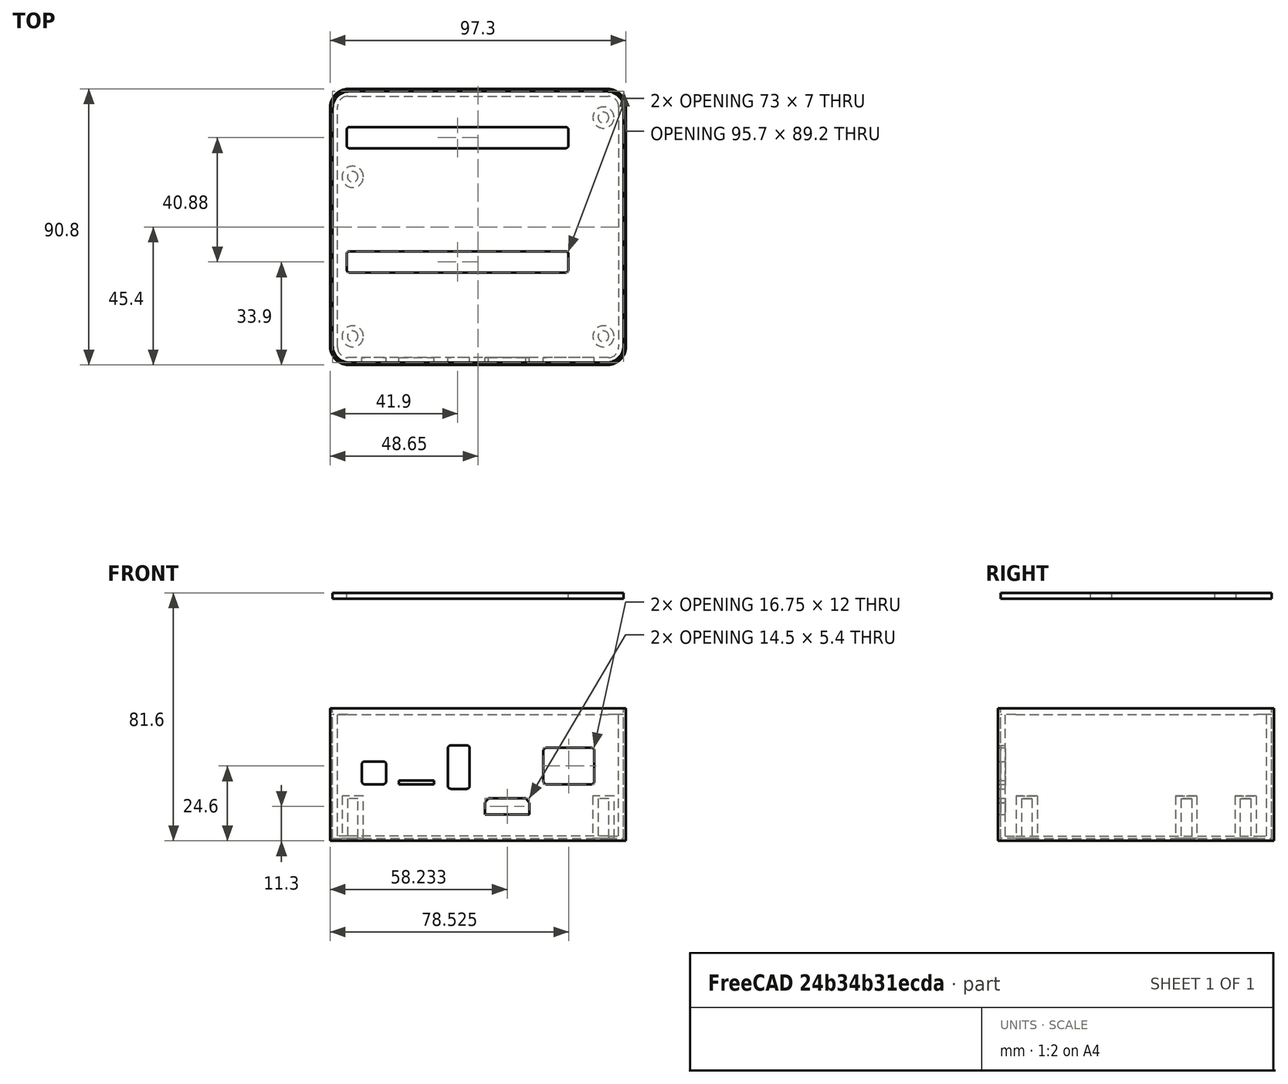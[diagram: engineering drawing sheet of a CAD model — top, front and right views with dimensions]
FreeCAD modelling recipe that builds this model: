
FCSTD DOCUMENT  (FreeCAD 0.16R6712 (Git))
Label: odroid-hc4-enclosure
License: All rights reserved
LicenseURL: http://en.wikipedia.org/wiki/All_rights_reserved
objects: Sketcher::SketchObject×7, PartDesign::Pad×6, Part::Thickness×2, Part::Cut×2, PartDesign::Fillet×1, Mesh::Feature×1, Part::Part2DObjectPython×1
note: 25 computed .brp shape members not serialized (recipe doc carries the construction recipe); baked Part::Feature solids carry a one-line shape summary decoded from their .brp

FEATURE [Sketcher::SketchObject] Sketch  label="Sketch - Board"
  expr: Constraints[50] = Sketch.Constraints.SataX
  expr: Constraints[51] = Sketch.Constraints.SataY
  expr: Constraints[52] = Sketch.Constraints.SataOffsetX
  sketch-geometry (20):
    g0: LineSegment StartX=-39.25 StartY=42 StartZ=0 EndX=39.25 EndY=42 EndZ=0
    g1: LineSegment StartX=45.25 StartY=36 StartZ=0 EndX=45.25 EndY=-36 EndZ=0
    g2: LineSegment StartX=39.25 StartY=-42 StartZ=0 EndX=-39.25 EndY=-42 EndZ=0
    g3: LineSegment StartX=-45.25 StartY=-36 StartZ=0 EndX=-45.25 EndY=36 EndZ=0
    g4: ArcOfCircle CenterX=-39.25 CenterY=-36 CenterZ=0 NormalX=0 NormalY=0 NormalZ=1 Radius=6 StartAngle=3.14159 EndAngle=4.71239
    g5: ArcOfCircle CenterX=39.25 CenterY=-36 CenterZ=0 NormalX=0 NormalY=0 NormalZ=1 Radius=6 StartAngle=4.71239 EndAngle=6.28319
    g6: ArcOfCircle CenterX=39.25 CenterY=36 CenterZ=0 NormalX=0 NormalY=0 NormalZ=1 Radius=6 StartAngle=0 EndAngle=1.5708
    g7: ArcOfCircle CenterX=-39.25 CenterY=36 CenterZ=0 NormalX=0 NormalY=0 NormalZ=1 Radius=6 StartAngle=1.5708 EndAngle=3.14159
    g8: Circle CenterX=-41.25 CenterY=-36 CenterZ=0 NormalX=0 NormalY=0 NormalZ=1 Radius=1.75
    g9: Circle CenterX=41.25 CenterY=-36 CenterZ=0 NormalX=0 NormalY=0 NormalZ=1 Radius=1.75
    g10: Circle CenterX=-41.25 CenterY=16.5 CenterZ=0 NormalX=0 NormalY=0 NormalZ=1 Radius=1.75
    g11: Circle CenterX=41.25 CenterY=36 CenterZ=0 NormalX=0 NormalY=0 NormalZ=1 Radius=1.75
    g12: LineSegment StartX=-24.4 StartY=-9 StartZ=0 EndX=19.25 EndY=-9 EndZ=0
    g13: LineSegment StartX=19.25 StartY=-9 StartZ=0 EndX=19.25 EndY=-14 EndZ=0
    g14: LineSegment StartX=19.25 StartY=-14 StartZ=0 EndX=-24.4 EndY=-14 EndZ=0
    g15: LineSegment StartX=-24.4 StartY=-14 StartZ=0 EndX=-24.4 EndY=-9 EndZ=0
    g16: LineSegment StartX=-24.4 StartY=31.88 StartZ=0 EndX=19.25 EndY=31.88 EndZ=0
    g17: LineSegment StartX=19.25 StartY=31.88 StartZ=0 EndX=19.25 EndY=26.88 EndZ=0
    g18: LineSegment StartX=19.25 StartY=26.88 StartZ=0 EndX=-24.4 EndY=26.88 EndZ=0
    g19: LineSegment StartX=-24.4 StartY=26.88 StartZ=0 EndX=-24.4 EndY=31.88 EndZ=0
  constraints (54):
    c: Horizontal(g0)
    c: Horizontal(g2)
    c: Vertical(g1)
    c: Vertical(g3)
    c: Tangent(g3,g4) = 1.5708
    c: Tangent(g2,g4) = 1.5708
    c: Tangent(g2,g5) = 1.5708
    c: Tangent(g1,g5) = 1.5708
    c: Tangent(g0,g6) = 1.5708
    c: Tangent(g1,g6) = 1.5708
    c: Tangent(g3,g7) = 1.5708
    c: Tangent(g0,g7) = 1.5708
    c: Symmetric(g3,g1,g-2)
    c: Symmetric(g2,g0,g-1)
    c: Radius(g6) = 6
    c: Equal(g6,g7)
    c: DistanceX(g3,g1) = 90.5  'X'
    c: DistanceY(g2,g0) = 84  'Y'
    c: Radius(g9) = 1.75  'Constraint20'
    c: Equal(g9,g8)
    c: Equal(g9,g10)
    c: Equal(g9,g11)
    c: DistanceY(g2,g9) = 6  'Y1'
    c: DistanceX(g9,g1) = 4  'X1'
    c: DistanceY(g2,g8) = 6  'Y4'
    c: DistanceX(g3,g8) = 4  'X4'
    c: DistanceX(g11,g1) = 4  'X2'
    c: DistanceY(g11,g0) = 6  'Y2'
    c: DistanceX(g3,g10) = 4  'X3'
    c: DistanceY(g10,g0) = 25.5  'Y3'
    c: Coincident(g12,g13)
    c: Coincident(g13,g14)
    c: Coincident(g14,g15)
    c: Coincident(g15,g12)
    c: Horizontal(g12)
    c: Horizontal(g14)
    c: Vertical(g13)
    c: Vertical(g15)
    c: DistanceX(g14,g13) = 43.65  'SataX'
    c: DistanceX(g13,g1) = 26  'SataOffsetX'
    c: DistanceY(g14,g12) = 5  'SataY'
    c: DistanceY(g2,g13) = 28  'SataoffsetY'
    c: Coincident(g16,g17)
    c: Coincident(g17,g18)
    c: Coincident(g18,g19)
    c: Coincident(g19,g16)
    c: Horizontal(g16)
    c: Horizontal(g18)
    c: Vertical(g17)
    c: Vertical(g19)
    c: DistanceX(g18,g17) = 43.65
    c: DistanceY(g18,g16) = 5
    c: DistanceX(g17,g1) = 26
    c: DistanceY(g16,g0) = 10.12  'Sata2OffsetY'
FEATURE [Sketcher::SketchObject] Sketch001  label="Sketch - Walls"
  expr: Constraints.X = Sketch.Constraints.X + 2 + 3.2 + 1.6
  expr: Constraints.Y = Sketch.Constraints.Y + 2 + 3.2 + 1.6
  sketch-geometry (8):
    g0: LineSegment StartX=-42.65 StartY=45.4 StartZ=0 EndX=42.65 EndY=45.4 EndZ=0
    g1: LineSegment StartX=48.65 StartY=39.4 StartZ=0 EndX=48.65 EndY=-39.4 EndZ=0
    g2: LineSegment StartX=42.65 StartY=-45.4 StartZ=0 EndX=-42.65 EndY=-45.4 EndZ=0
    g3: LineSegment StartX=-48.65 StartY=-39.4 StartZ=0 EndX=-48.65 EndY=39.4 EndZ=0
    g4: ArcOfCircle CenterX=-42.65 CenterY=-39.4 CenterZ=0 NormalX=0 NormalY=0 NormalZ=1 Radius=6 StartAngle=3.14159 EndAngle=4.71239
    g5: ArcOfCircle CenterX=42.65 CenterY=-39.4 CenterZ=0 NormalX=0 NormalY=0 NormalZ=1 Radius=6 StartAngle=4.71239 EndAngle=6.28319
    g6: ArcOfCircle CenterX=42.65 CenterY=39.4 CenterZ=0 NormalX=0 NormalY=0 NormalZ=1 Radius=6 StartAngle=0 EndAngle=1.5708
    g7: ArcOfCircle CenterX=-42.65 CenterY=39.4 CenterZ=0 NormalX=0 NormalY=0 NormalZ=1 Radius=6 StartAngle=1.5708 EndAngle=3.14159
  constraints (19):
    c: Horizontal(g0)
    c: Horizontal(g2)
    c: Vertical(g1)
    c: Vertical(g3)
    c: Tangent(g3,g4) = 1.5708
    c: Tangent(g2,g4) = 1.5708
    c: Tangent(g2,g5) = 1.5708
    c: Tangent(g1,g5) = 1.5708
    c: Tangent(g1,g6) = 1.5708
    c: Tangent(g0,g6) = 1.5708
    c: Tangent(g3,g7) = 1.5708
    c: Tangent(g0,g7) = 1.5708
    c: Radius(g7) = 6
    c: Equal(g7,g6)
    c: Equal(g7,g5)
    c: DistanceX(g3,g1) = 97.3  'X'
    c: DistanceY(g2,g0) = 90.8  'Y'
    c: Symmetric(g2,g0,g-1)  'Constraint18'
    c: Symmetric(g3,g1,g-2)
FEATURE [PartDesign::Pad] Pad
  Length = 42
  Length2 = 1.6
  Sketch = -> Sketch001
  Type = 4
FEATURE [Part::Thickness] Thickness
  Faces = -> Pad [Face10]
  Intersection = false
  Join = 0
  Mode = 0
  SelfIntersection = false
  Value = -0.8
FEATURE [Sketcher::SketchObject] Sketch002  label="Sketch - Legs"
  Placement = pos=(0,0,-0.8) rot=(0,0,1;0rad)
  Support = -> Thickness [Face19]
  expr: Constraints[24] = Sketch.Constraints.Y4
  expr: Constraints[29] = Sketch.Constraints.Y3
  expr: Constraints[28] = Sketch.Constraints.X3
  expr: Constraints[26] = Sketch.Constraints.X2
  expr: Constraints[27] = Sketch.Constraints.Y2
  expr: Constraints[25] = Sketch.Constraints.X4
  expr: Constraints[22] = Sketch.Constraints.Y1
  expr: Constraints.Y = Sketch.Constraints.Y
  expr: Constraints[23] = Sketch.Constraints.X1
  expr: Constraints.X = Sketch.Constraints.X
  sketch-geometry (12):
    g0: LineSegment [constr] StartX=-39.25 StartY=42 StartZ=0 EndX=39.25 EndY=42 EndZ=0
    g1: LineSegment [constr] StartX=45.25 StartY=36 StartZ=0 EndX=45.25 EndY=-36 EndZ=0
    g2: LineSegment [constr] StartX=39.25 StartY=-42 StartZ=0 EndX=-39.25 EndY=-42 EndZ=0
    g3: LineSegment [constr] StartX=-45.25 StartY=-36 StartZ=0 EndX=-45.25 EndY=36 EndZ=0
    g4: ArcOfCircle [constr] CenterX=-39.25 CenterY=-36 CenterZ=0 NormalX=0 NormalY=0 NormalZ=1 Radius=6 StartAngle=3.14159 EndAngle=4.71239
    g5: ArcOfCircle [constr] CenterX=39.25 CenterY=-36 CenterZ=0 NormalX=0 NormalY=0 NormalZ=1 Radius=6 StartAngle=4.71239 EndAngle=6.28319
    g6: ArcOfCircle [constr] CenterX=39.25 CenterY=36 CenterZ=0 NormalX=0 NormalY=0 NormalZ=1 Radius=6 StartAngle=0 EndAngle=1.5708
    g7: ArcOfCircle [constr] CenterX=-39.25 CenterY=36 CenterZ=0 NormalX=0 NormalY=0 NormalZ=1 Radius=6 StartAngle=1.5708 EndAngle=3.14159
    g8: Circle CenterX=-41.25 CenterY=-36 CenterZ=0 NormalX=0 NormalY=0 NormalZ=1 Radius=1.75
    g9: Circle CenterX=41.25 CenterY=-36 CenterZ=0 NormalX=0 NormalY=0 NormalZ=1 Radius=1.75
    g10: Circle CenterX=-41.25 CenterY=16.5 CenterZ=0 NormalX=0 NormalY=0 NormalZ=1 Radius=1.75
    g11: Circle CenterX=41.25 CenterY=36 CenterZ=0 NormalX=0 NormalY=0 NormalZ=1 Radius=1.75
  constraints (30):
    c: Horizontal(g0)
    c: Horizontal(g2)
    c: Vertical(g1)
    c: Vertical(g3)
    c: Tangent(g3,g4) = 1.5708
    c: Tangent(g2,g4) = 1.5708
    c: Tangent(g2,g5) = 1.5708
    c: Tangent(g1,g5) = 1.5708
    c: Tangent(g0,g6) = 1.5708
    c: Tangent(g1,g6) = 1.5708
    c: Tangent(g3,g7) = 1.5708
    c: Tangent(g0,g7) = 1.5708
    c: Symmetric(g3,g1,g-2)
    c: Symmetric(g2,g0,g-1)
    c: Radius(g6) = 6
    c: Equal(g6,g7)
    c: DistanceX(g3,g1) = 90.5  'X'
    c: DistanceY(g2,g0) = 84  'Y'
    c: Radius(g9) = 1.75  'Constraint20'
    c: Equal(g9,g8)
    c: Equal(g9,g10)
    c: Equal(g9,g11)
    c: DistanceY(g2,g9) = 6
    c: DistanceX(g9,g1) = 4
    c: DistanceY(g2,g8) = 6
    c: DistanceX(g3,g8) = 4
    c: DistanceX(g11,g1) = 4
    c: DistanceY(g11,g0) = 6
    c: DistanceX(g3,g10) = 4
    c: DistanceY(g10,g0) = 25.5
FEATURE [PartDesign::Pad] Pad001
  Length = 13
  Length2 = 100
  Sketch = -> Sketch002
  Type = 0
FEATURE [Sketcher::SketchObject] Sketch003  label="Sketch - Wide Legs"
  ExternalGeometry = -> [Pad001]
  Placement = pos=(0,0,-0.8) rot=(0,0,1;0rad)
  Support = -> Pad001 [Face19]
  sketch-geometry (4):
    g0: Circle CenterX=41.25 CenterY=-36 CenterZ=0 NormalX=0 NormalY=0 NormalZ=1 Radius=3.5
    g1: Circle CenterX=41.25 CenterY=36 CenterZ=0 NormalX=0 NormalY=0 NormalZ=1 Radius=3.5
    g2: Circle CenterX=-41.25 CenterY=16.5 CenterZ=0 NormalX=0 NormalY=0 NormalZ=1 Radius=3.5
    g3: Circle CenterX=-41.25 CenterY=-36 CenterZ=0 NormalX=0 NormalY=0 NormalZ=1 Radius=3.5
  constraints (4):
    c: Radius(g2) = 3.5
    c: Equal(g2,g1)
    c: Equal(g2,g0)
    c: Equal(g2,g3)
FEATURE [PartDesign::Pad] Pad002
  Length = 14
  Length2 = 100
  Sketch = -> Sketch003
  Type = 0
FEATURE [Sketcher::SketchObject] Sketch004
  Placement = pos=(0,-46.2,0) rot=(1,0,0;1.5708rad)
  sketch-geometry (40):
    g0: LineSegment StartX=22.5 StartY=29 StartZ=0 EndX=37.25 EndY=29 EndZ=0
    g1: LineSegment StartX=38.25 StartY=28 StartZ=0 EndX=38.25 EndY=18 EndZ=0
    g2: LineSegment StartX=37.25 StartY=17 StartZ=0 EndX=22.5 EndY=17 EndZ=0
    g3: LineSegment StartX=21.5 StartY=18 StartZ=0 EndX=21.5 EndY=28 EndZ=0
    g4: LineSegment StartX=-8.95 StartY=29.8 StartZ=0 EndX=-3.75 EndY=29.8 EndZ=0
    g5: LineSegment StartX=-2.75 StartY=28.8 StartZ=0 EndX=-2.75 EndY=16.5 EndZ=0
    g6: LineSegment StartX=-3.75 StartY=15.5 StartZ=0 EndX=-8.95 EndY=15.5 EndZ=0
    g7: LineSegment StartX=-9.95 StartY=16.5 StartZ=0 EndX=-9.95 EndY=28.8 EndZ=0
    g8: LineSegment StartX=-37.25 StartY=24.5 StartZ=0 EndX=-31.25 EndY=24.5 EndZ=0
    g9: LineSegment StartX=-30.25 StartY=23.5 StartZ=0 EndX=-30.25 EndY=18 EndZ=0
    g10: LineSegment StartX=-31.25 StartY=17 StartZ=0 EndX=-37.25 EndY=17 EndZ=0
    g11: LineSegment StartX=-38.25 StartY=18 StartZ=0 EndX=-38.25 EndY=23.5 EndZ=0
    g12: LineSegment StartX=-26 StartY=18.25 StartZ=0 EndX=-14.5 EndY=18.25 EndZ=0
    g13: LineSegment StartX=-14.5 StartY=18.25 StartZ=0 EndX=-14.5 EndY=17 EndZ=0
    g14: LineSegment StartX=-14.5 StartY=17 StartZ=0 EndX=-26 EndY=17 EndZ=0
    g15: LineSegment StartX=-26 StartY=17 StartZ=0 EndX=-26 EndY=18.25 EndZ=0
    g16: ArcOfCircle CenterX=37.25 CenterY=18 CenterZ=0 NormalX=0 NormalY=0 NormalZ=1 Radius=1 StartAngle=4.71239 EndAngle=6.28319
    g17: ArcOfCircle CenterX=37.25 CenterY=28 CenterZ=0 NormalX=0 NormalY=0 NormalZ=1 Radius=1 StartAngle=0 EndAngle=1.5708
    g18: ArcOfCircle CenterX=22.5 CenterY=28 CenterZ=0 NormalX=0 NormalY=0 NormalZ=1 Radius=1 StartAngle=1.5708 EndAngle=3.14159
    g19: ArcOfCircle CenterX=22.5 CenterY=18 CenterZ=0 NormalX=0 NormalY=0 NormalZ=1 Radius=1 StartAngle=3.14159 EndAngle=4.71239
    g20: ArcOfCircle CenterX=-8.95 CenterY=16.5 CenterZ=0 NormalX=0 NormalY=0 NormalZ=1 Radius=1 StartAngle=3.14159 EndAngle=4.71239
    g21: ArcOfCircle CenterX=-3.75 CenterY=16.5 CenterZ=0 NormalX=0 NormalY=0 NormalZ=1 Radius=1 StartAngle=4.71239 EndAngle=6.28319
    g22: ArcOfCircle CenterX=-3.75 CenterY=28.8 CenterZ=0 NormalX=0 NormalY=0 NormalZ=1 Radius=1 StartAngle=0 EndAngle=1.5708
    g23: ArcOfCircle CenterX=-8.95 CenterY=28.8 CenterZ=0 NormalX=0 NormalY=0 NormalZ=1 Radius=1 StartAngle=1.5708 EndAngle=3.14159
    g24: ArcOfCircle CenterX=-37.25 CenterY=18 CenterZ=0 NormalX=0 NormalY=0 NormalZ=1 Radius=1 StartAngle=3.14159 EndAngle=4.71239
    g25: ArcOfCircle CenterX=-31.25 CenterY=18 CenterZ=0 NormalX=0 NormalY=0 NormalZ=1 Radius=1 StartAngle=4.71239 EndAngle=6.28319
    g26: ArcOfCircle CenterX=-31.25 CenterY=23.5 CenterZ=0 NormalX=0 NormalY=0 NormalZ=1 Radius=1 StartAngle=0 EndAngle=1.5708
    g27: ArcOfCircle CenterX=-37.25 CenterY=23.5 CenterZ=0 NormalX=0 NormalY=0 NormalZ=1 Radius=1 StartAngle=1.5708 EndAngle=3.14159
    g28: GeomPoint [constr] X=2.3334 Y=7 Z=0
    g29: GeomPoint [constr] X=16.8334 Y=7 Z=0
    g30: GeomPoint [constr] X=2.3334 Y=11.0069 Z=0
    g31: GeomPoint [constr] X=3.39176 Y=12.4 Z=0
    g32: GeomPoint [constr] X=15.7519 Y=12.4 Z=0
    g33: GeomPoint [constr] X=16.8334 Y=10.8557 Z=0
    g34: LineSegment StartX=2.3334 StartY=7 StartZ=0 EndX=2.3334 EndY=11.0069 EndZ=0
    g35: LineSegment StartX=2.3334 StartY=11.0069 StartZ=0 EndX=3.39176 EndY=12.4 EndZ=0
    g36: LineSegment StartX=3.39176 StartY=12.4 StartZ=0 EndX=15.7519 EndY=12.4 EndZ=0
    g37: LineSegment StartX=15.7519 StartY=12.4 StartZ=0 EndX=16.8334 EndY=10.8557 EndZ=0
    g38: LineSegment StartX=16.8334 StartY=10.8557 StartZ=0 EndX=16.8334 EndY=7 EndZ=0
    g39: LineSegment StartX=16.8334 StartY=7 StartZ=0 EndX=2.3334 EndY=7 EndZ=0
  constraints (91):
    c: Horizontal(g0)
    c: Horizontal(g2)
    c: Vertical(g1)
    c: Vertical(g3)
    c: Horizontal(g4)
    c: Horizontal(g6)
    c: Vertical(g5)
    c: Vertical(g7)
    c: Horizontal(g8)
    c: Horizontal(g10)
    c: Vertical(g9)
    c: Vertical(g11)
    c: Coincident(g12,g13)
    c: Coincident(g13,g14)
    c: Coincident(g14,g15)
    c: Coincident(g15,g12)
    c: Horizontal(g12)
    c: Horizontal(g14)
    c: Vertical(g13)
    c: Vertical(g15)
    c: DistanceX(g14,g-1) = 26
    c: DistanceX(g14,g14) = 11.5
    c: Tangent(g2,g16) = 1.5708
    c: Tangent(g1,g16) = 1.5708
    c: Tangent(g0,g17) = 1.5708
    c: Tangent(g1,g17) = 1.5708
    c: Tangent(g3,g18) = 1.5708
    c: Tangent(g0,g18) = 1.5708
    c: Tangent(g3,g19) = 1.5708
    c: Tangent(g2,g19) = 1.5708
    c: DistanceX(g-1,g1) = 38.25
    c: DistanceX(g3,g1) = 16.75
    c: DistanceY(g2,g0) = 12
    c: DistanceY(g-1,g2) = 17
    c: Radius(g17) = 1
    c: Equal(g17,g16)
    c: Equal(g17,g19)
    c: Equal(g17,g18)
    c: Tangent(g7,g20) = 1.5708
    c: Tangent(g6,g20) = 1.5708
    c: Tangent(g6,g21) = 1.5708
    c: Tangent(g5,g21) = 1.5708
    c: Tangent(g4,g22) = 1.5708
    c: Tangent(g5,g22) = 1.5708
    c: Tangent(g7,g23) = 1.5708
    c: Tangent(g4,g23) = 1.5708
    c: DistanceX(g5,g-1) = 2.75
    c: DistanceY(g-1,g6) = 15.5
    c: DistanceX(g7,g5) = 7.2
    c: DistanceY(g6,g4) = 14.3
    c: Radius(g21) = 1
    c: Equal(g21,g22)
    c: Equal(g21,g23)
    c: Equal(g21,g20)
    c: Tangent(g11,g24) = 1.5708
    c: Tangent(g10,g24) = 1.5708
    c: Tangent(g10,g25) = 1.5708
    c: Tangent(g9,g25) = 1.5708
    c: Tangent(g9,g26) = 1.5708
    c: Tangent(g8,g26) = 1.5708
    c: Tangent(g11,g27) = 1.5708
    c: Tangent(g8,g27) = 1.5708
    c: DistanceX(g9,g-1) = 30.25
    c: DistanceY(g10,g8) = 7.5
    c: DistanceX(g11,g9) = 8
    c: DistanceY(g-1,g10) = 17
    c: Radius(g25) = 1
    c: Equal(g25,g24)
    c: Equal(g25,g27)
    c: Equal(g25,g26)
    c: DistanceY(g-1,g14) = 17
    c: DistanceY(g14,g12) = 1.25
    c: Coincident(g34,g28)
    c: Coincident(g34,g30)
    c: Vertical(g34)
    c: Coincident(g34,g35)
    c: Coincident(g35,g31)
    c: Coincident(g35,g36)
    c: Coincident(g36,g32)
    c: Horizontal(g36)
    c: Coincident(g36,g37)
    c: Coincident(g37,g33)
    c: Coincident(g37,g38)
    c: Coincident(g38,g29)
    c: Vertical(g38)
    c: Coincident(g38,g39)
    c: Coincident(g39,g34)
    c: Horizontal(g39)
    c: DistanceX(g28,g29) = 14.5
    c: DistanceY(g-1,g28) = 7
    c: DistanceY(g28,g31) = 5.4
FEATURE [PartDesign::Pad] Pad003
  Length = 3.2
  Length2 = 100
  Placement = pos=(0,-46.2,0) rot=(1,0,0;1.5708rad)
  Reversed = true
  Sketch = -> Sketch004
  Type = 0
FEATURE [Part::Cut] Cut
  Base = -> Pad002
  Tool = -> Pad003
FEATURE [PartDesign::Fillet] Fillet
  Base = -> Cut [Edge3,Edge9,Edge11,Edge12,Edge13,Edge14,Edge15,Edge6]
  Radius = 0.6
FEATURE [Mesh::Feature] Odroid_HC4  label="Odroid-HC4"
  Placement = pos=(-45.25,-42,13) rot=(0,0,1;0rad)
FEATURE [Sketcher::SketchObject] Sketch005  label="Sketch - Top Lid"
  Placement = pos=(0,0,42) rot=(0,0,1;0rad)
  Support = -> Pad [Face10]
  expr: Constraints[58] = Sketch.Constraints.Sata2OffsetY + 1 + 1.6 - 1
  expr: Constraints.Y = Sketch.Constraints.Y + 2 + 3.2
  expr: Constraints.X = Sketch.Constraints.X + 2 + 3.2
  sketch-geometry (24):
    g0: LineSegment StartX=-42.35 StartY=44.6 StartZ=0 EndX=42.35 EndY=44.6 EndZ=0
    g1: LineSegment StartX=47.85 StartY=39.1 StartZ=0 EndX=47.85 EndY=-39.1 EndZ=0
    g2: LineSegment StartX=42.35 StartY=-44.6 StartZ=0 EndX=-42.35 EndY=-44.6 EndZ=0
    g3: LineSegment StartX=-47.85 StartY=-39.1 StartZ=0 EndX=-47.85 EndY=39.1 EndZ=0
    g4: ArcOfCircle CenterX=-42.35 CenterY=-39.1 CenterZ=0 NormalX=0 NormalY=0 NormalZ=1 Radius=5.5 StartAngle=3.14159 EndAngle=4.71239
    g5: ArcOfCircle CenterX=42.35 CenterY=-39.1 CenterZ=0 NormalX=0 NormalY=0 NormalZ=1 Radius=5.5 StartAngle=4.71239 EndAngle=6.28319
    g6: ArcOfCircle CenterX=42.35 CenterY=39.1 CenterZ=0 NormalX=0 NormalY=0 NormalZ=1 Radius=5.5 StartAngle=0 EndAngle=1.5708
    g7: ArcOfCircle CenterX=-42.35 CenterY=39.1 CenterZ=0 NormalX=0 NormalY=0 NormalZ=1 Radius=5.5 StartAngle=1.5708 EndAngle=3.14159
    g8: LineSegment StartX=-42.25 StartY=-8 StartZ=0 EndX=28.75 EndY=-8 EndZ=0
    g9: LineSegment StartX=29.75 StartY=-9 StartZ=0 EndX=29.75 EndY=-14 EndZ=0
    g10: LineSegment StartX=28.75 StartY=-15 StartZ=0 EndX=-42.25 EndY=-15 EndZ=0
    g11: LineSegment StartX=-43.25 StartY=-14 StartZ=0 EndX=-43.25 EndY=-9 EndZ=0
    g12: ArcOfCircle CenterX=-42.25 CenterY=-9 CenterZ=0 NormalX=0 NormalY=0 NormalZ=1 Radius=1 StartAngle=1.5708 EndAngle=3.14159
    g13: ArcOfCircle CenterX=-42.25 CenterY=-14 CenterZ=0 NormalX=0 NormalY=0 NormalZ=1 Radius=1 StartAngle=3.14159 EndAngle=4.71239
    g14: ArcOfCircle CenterX=28.75 CenterY=-14 CenterZ=0 NormalX=0 NormalY=0 NormalZ=1 Radius=1 StartAngle=4.71239 EndAngle=6.28319
    g15: ArcOfCircle CenterX=28.75 CenterY=-9 CenterZ=0 NormalX=0 NormalY=0 NormalZ=1 Radius=1 StartAngle=0 EndAngle=1.5708
    g16: LineSegment StartX=-42.25 StartY=32.88 StartZ=0 EndX=28.75 EndY=32.88 EndZ=0
    g17: LineSegment StartX=29.75 StartY=31.88 StartZ=0 EndX=29.75 EndY=26.88 EndZ=0
    g18: LineSegment StartX=28.75 StartY=25.88 StartZ=0 EndX=-42.25 EndY=25.88 EndZ=0
    g19: LineSegment StartX=-43.25 StartY=26.88 StartZ=0 EndX=-43.25 EndY=31.88 EndZ=0
    g20: ArcOfCircle CenterX=28.75 CenterY=26.88 CenterZ=0 NormalX=0 NormalY=0 NormalZ=1 Radius=1 StartAngle=4.71239 EndAngle=6.28319
    g21: ArcOfCircle CenterX=28.75 CenterY=31.88 CenterZ=0 NormalX=0 NormalY=0 NormalZ=1 Radius=1 StartAngle=0 EndAngle=1.5708
    g22: ArcOfCircle CenterX=-42.25 CenterY=31.88 CenterZ=0 NormalX=0 NormalY=0 NormalZ=1 Radius=1 StartAngle=1.5708 EndAngle=3.14159
    g23: ArcOfCircle CenterX=-42.25 CenterY=26.88 CenterZ=0 NormalX=0 NormalY=0 NormalZ=1 Radius=1 StartAngle=3.14159 EndAngle=4.71239
  constraints (59):
    c: Horizontal(g0)
    c: Horizontal(g2)
    c: Vertical(g1)
    c: Vertical(g3)
    c: Tangent(g3,g4) = 1.5708
    c: Tangent(g2,g4) = 1.5708
    c: Tangent(g2,g5) = 1.5708
    c: Tangent(g1,g5) = 1.5708
    c: Tangent(g1,g6) = 1.5708
    c: Tangent(g0,g6) = 1.5708
    c: Tangent(g3,g7) = 1.5708
    c: Tangent(g0,g7) = 1.5708
    c: Radius(g7) = 5.5
    c: Equal(g7,g6)
    c: Equal(g7,g5)
    c: DistanceX(g3,g1) = 95.7  'X'
    c: DistanceY(g2,g0) = 89.2  'Y'
    c: Symmetric(g2,g0,g-1)  'Constraint18'
    c: Symmetric(g3,g1,g-2)
    c: Horizontal(g8)
    c: Horizontal(g10)
    c: Vertical(g9)
    c: Vertical(g11)
    c: Tangent(g11,g12) = 1.5708  'Constraint29'
    c: Tangent(g8,g12) = 1.5708  'Constraint25'
    c: Tangent(g11,g13) = 1.5708  'Constraint27'
    c: Tangent(g10,g13) = 1.5708
    c: Tangent(g10,g14) = 1.5708
    c: Tangent(g9,g14) = 1.5708
    c: Tangent(g8,g15) = 1.5708
    c: Tangent(g9,g15) = 1.5708
    c: DistanceY(g2,g10) = 29.6
    c: DistanceX(g9,g1) = 18.1
    c: DistanceY(g10,g8) = 7
    c: DistanceX(g11,g9) = 73
    c: Radius(g13) = 1
    c: Equal(g13,g12)
    c: Equal(g13,g15)
    c: Equal(g13,g14)
    c: Horizontal(g16)
    c: Horizontal(g18)
    c: Vertical(g17)
    c: Vertical(g19)
    c: Tangent(g18,g20) = 1.5708
    c: Tangent(g17,g20) = 1.5708
    c: Tangent(g16,g21) = 1.5708
    c: Tangent(g17,g21) = 1.5708
    c: Tangent(g19,g22) = 1.5708
    c: Tangent(g16,g22) = 1.5708
    c: Tangent(g19,g23) = 1.5708
    c: Tangent(g18,g23) = 1.5708
    c: Radius(g22) = 1
    c: Equal(g22,g23)
    c: Equal(g22,g20)
    c: Equal(g22,g21)
    c: DistanceY(g18,g16) = 7
    c: DistanceX(g19,g17) = 73
    c: DistanceX(g17,g1) = 18.1
    c: DistanceY(g16,g0) = 11.72
FEATURE [Part::Part2DObjectPython] Clone2D  label="Clone of Sketch - Top Lid (2D)"  # Draft 2D object (typed FeaturePython)
  Objects = -> [Sketch005]
  Placement = pos=(0,0,78) rot=(0,0,1;0rad)
  Scale = (1,1,1)
FEATURE [PartDesign::Pad] Pad004
  Length = 2
  Length2 = 100
  Placement = pos=(0,0,78) rot=(0,0,1;0rad)
  Sketch = -> Clone2D
  Type = 0
FEATURE [Sketcher::SketchObject] Sketch006  label="Sketch - Walls001"
  expr: Constraints.X = Sketch.Constraints.X + 2 + 3.2
  expr: Constraints.Y = Sketch.Constraints.Y + 2 + 3.2
  sketch-geometry (8):
    g0: LineSegment StartX=-42.85 StartY=44.6 StartZ=0 EndX=42.85 EndY=44.6 EndZ=0
    g1: LineSegment StartX=47.85 StartY=39.6 StartZ=0 EndX=47.85 EndY=-39.6 EndZ=0
    g2: LineSegment StartX=42.85 StartY=-44.6 StartZ=0 EndX=-42.85 EndY=-44.6 EndZ=0
    g3: LineSegment StartX=-47.85 StartY=-39.6 StartZ=0 EndX=-47.85 EndY=39.6 EndZ=0
    g4: ArcOfCircle CenterX=-42.85 CenterY=-39.6 CenterZ=0 NormalX=0 NormalY=0 NormalZ=1 Radius=5 StartAngle=3.14159 EndAngle=4.71239
    g5: ArcOfCircle CenterX=42.85 CenterY=-39.6 CenterZ=0 NormalX=0 NormalY=0 NormalZ=1 Radius=5 StartAngle=4.71239 EndAngle=6.28319
    g6: ArcOfCircle CenterX=42.85 CenterY=39.6 CenterZ=0 NormalX=0 NormalY=0 NormalZ=1 Radius=5 StartAngle=0 EndAngle=1.5708
    g7: ArcOfCircle CenterX=-42.85 CenterY=39.6 CenterZ=0 NormalX=0 NormalY=0 NormalZ=1 Radius=5 StartAngle=1.5708 EndAngle=3.14159
  constraints (19):
    c: Horizontal(g0)
    c: Horizontal(g2)
    c: Vertical(g1)
    c: Vertical(g3)
    c: Tangent(g3,g4) = 1.5708
    c: Tangent(g2,g4) = 1.5708
    c: Tangent(g2,g5) = 1.5708
    c: Tangent(g1,g5) = 1.5708
    c: Tangent(g1,g6) = 1.5708
    c: Tangent(g0,g6) = 1.5708
    c: Tangent(g3,g7) = 1.5708
    c: Tangent(g0,g7) = 1.5708
    c: Radius(g7) = 5
    c: Equal(g7,g6)
    c: Equal(g7,g5)
    c: DistanceX(g3,g1) = 95.7  'X'
    c: DistanceY(g2,g0) = 89.2  'Y'
    c: Symmetric(g2,g0,g-1)  'Constraint18'
    c: Symmetric(g3,g1,g-2)
FEATURE [PartDesign::Pad] Pad005
  Length = 40
  Length2 = 1.6
  Sketch = -> Sketch006
  Type = 4
FEATURE [Part::Thickness] Thickness001
  Faces = -> Pad005 [Face10]
  Intersection = false
  Join = 0
  Mode = 0
  SelfIntersection = false
  Value = -1.6
FEATURE [Part::Cut] Cut001
  Base = -> Thickness001
  Tool = -> Pad003
